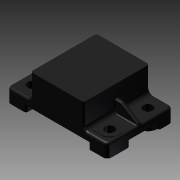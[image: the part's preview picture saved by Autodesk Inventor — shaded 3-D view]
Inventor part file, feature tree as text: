
AUTODESK INVENTOR PART (.ipt)
format: ipt  version: 2011 (Build 150239000, 239)  size: 423,424 bytes
history: native  units: mm (DEFAULTED — no unit token found)
features: sketch x12, extrude x11, fillet x5, mirror x3, plane x2, rib x1
ambient origin geometry x8: Origin, YZ Plane, XZ Plane, XY Plane, X Axis, Y Axis, Z Axis, Center Point
bodies: Solid1 (feature_tree)
feature tree (34):
  extrude  "Extrusion1"  Depth=5.08mm
  fillet  "Fillet19"  Radius=73.66mm
  extrude  "Extrusion4"  Depth=48.26mm TaperAngle=0.0deg
  fillet  "Fillet20"  Radius=3.048mm
  extrude  "Extrusion10"  Depth=1.524mm
  extrude  "Extrusion12"  Depth=10.16mm
  fillet  "Fillet21"  Radius=8.255mm
  plane  "Work Plane3"
  plane  "Work Plane4"
  mirror  "Mirror4"
  mirror  "Mirror5"
  extrude  "Extrusion11"  Depth=0.381mm TaperAngle=0.0deg
  extrude  "Extrusion13"  Depth=3.302mm
  extrude  "Extrusion14"  Depth=8.636mm
  extrude  "Extrusion15"  Depth=2.54mm
  extrude  "Extrusion16"  Depth=0.762mm
  extrude  "Extrusion5"  Depth=3.048mm
  extrude  "Extrusion6"  Depth=13.97mm
  rib  "Rib2"
  fillet  "Fillet22"  Radius=16.51mm
  fillet  "Fillet23"  Radius=4.826mm
  mirror  "Mirror6"
  sketch  "Sketch1"  dims[d1=23.099032mm d2=5.08mm d3=73.66mm]
  sketch  "Sketch5"  dims[d4=38.862mm d5=48.26mm d6=0.0mm d40=3.048mm]
  sketch  "Sketch6"  dims[d41=3.048mm d42=1.524mm]
  sketch  "Sketch7"  dims[d43=6.858mm d44=10.16mm d45=8.255mm]
  sketch  "Sketch8"  dims[d46=8.89mm d47=0.0mm d48=0.381mm d49=0.0mm]
  sketch  "Sketch14"  dims[d50=0.381mm d51=0.0mm d52=3.302mm]
  sketch  "Sketch15"  dims[d53=3.302mm d54=8.636mm]
  sketch  "Sketch16"  dims[d55=3.302mm d56=2.54mm]
  sketch  "Sketch17"  dims[d57=2.54mm d58=0.762mm]
  sketch  "Sketch18"  dims[d59=0.762mm d83=3.048mm]
  sketch  "Sketch19"  dims[d84=1.524mm d85=13.97mm d86=16.51mm d87=4.826mm d88=0.0mm]
  sketch  "Sketch20"  dims[d89=1.27mm d90=4.826mm d91=0.0mm d92=3.048mm d93=1.524mm d94=16.51mm d95=13.97mm d96=4.826mm d97=0.0mm d98=1.27mm d99=4.826mm d100=0.0mm d101=13.97mm d102=13.97mm d103=3.048mm d104=1.524mm d105=1.016mm d106=3.048mm d107=1.524mm d108=1.016mm d109=13.97mm d110=4.826mm d111=0.0mm d112=1.27mm d113=1.27mm d114=0.381mm d116=0.381mm d117=13.97mm d118=4.826mm d119=0.0mm d120=1.27mm d121=0.381mm d122=0.381mm d124=13.97mm d125=4.826mm d126=0.0mm]
